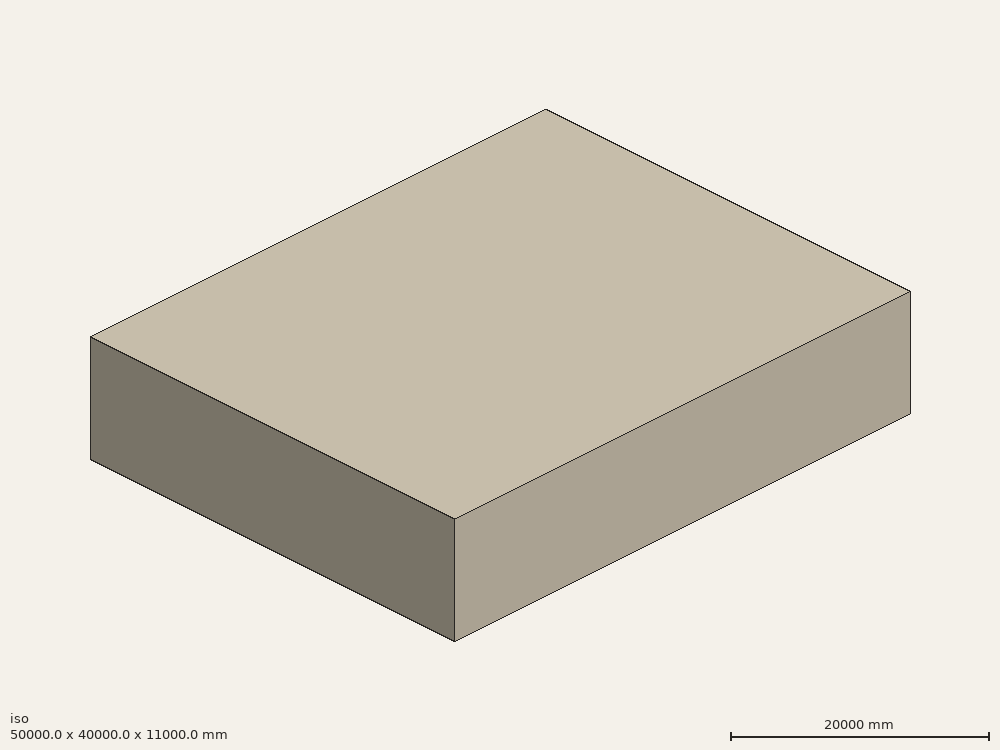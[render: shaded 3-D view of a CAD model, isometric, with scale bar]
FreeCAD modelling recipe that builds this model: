
FCSTD DOCUMENT  (FreeCAD 0.20R29603 (Git))
Label: windforces_cfMesh_hause
License: All rights reserved
LicenseURL: http://en.wikipedia.org/wiki/All_rights_reserved
objects: Part::FeaturePython×10, Part::Feature×4, Part::Box×3, App::DocumentObjectGroupPython×2, Mesh::Feature×1, Part::MultiFuse×1, Part::Cut×1, App::MaterialObjectPython×1
note: 19 computed .brp shape members not serialized (recipe doc carries the construction recipe); baked Part::Feature solids carry a one-line shape summary decoded from their .brp

FEATURE [Mesh::Feature] cfdwindforce
FEATURE [Part::Feature] cfdwindforce001
  shape: bbox 15090 x 17300 x 3871 mm, 94 faces, 0 solids (baked)
FEATURE [Part::Feature] cfdwindforce001_solid  label="cfdwindforce001 (Solid)"
  Placement = pos=(-7500,-8500,0) rot=(0,0,1;0rad)
  shape: bbox 15090 x 17300 x 3871 mm, 94 faces (baked)
FEATURE [Part::Box] Box  label="Cube"
  AttacherType = Attacher::AttachEngine3D
  Height = 11000
  Length = 50000
  Placement = pos=(-25000,-20000,0) rot=(0,0,1;0rad)
  Width = 40000
FEATURE [Part::Box] Box001  label="Cube001"
  AttacherType = Attacher::AttachEngine3D
  Height = 1400
  Length = 70
  Placement = pos=(4750,-7000,4000) rot=(0,1,0;1.0472rad)
  Width = 15000
FEATURE [Part::Feature] Box001001  label="Cube002"
  Placement = pos=(250,-7000,4000) rot=(0,1,0;1.0472rad)
  shape: bbox 1247 x 15000 x 760.6 mm, 6 faces (baked)
FEATURE [Part::Feature] Box001002  label="Cube003"
  Placement = pos=(2500,-7000,4000) rot=(0,1,0;1.0472rad)
  shape: bbox 1247 x 15000 x 760.6 mm, 6 faces (baked)
FEATURE [Part::Box] Box001003  label="refinement"
  AttacherType = Attacher::AttachEngine3D
  Height = 7000
  Length = 20000
  Placement = pos=(-10000,-11000,0) rot=(0,0,1;0rad)
  Width = 22000
FEATURE [Part::MultiFuse] Fusion
  Shapes = -> [cfdwindforce001_solid,Box001,Box001001,Box001002]
FEATURE [Part::Cut] Cut  label="building_model"
  Base = -> Box
  Tool = -> Fusion
FEATURE [Part::FeaturePython] PhysicsModel  # WARN: FeaturePython — macro-defined, semantics opaque (R4)
  Flow = 0
  Phase = 0
  SRFModelAxis = (0,0,0)
  SRFModelCoR = (0,0,0)
  SRFModelEnabled = false
  SRFModelRPM = 0
  Time = 0
  Turbulence = 3
  TurbulenceModel = 1
  gx = 0
  gy = -9800
  gz = 0
FEATURE [App::MaterialObjectPython] FluidProperties  # material (typed FeaturePython)
  Category = 1
  Material = CardName=AirIsothermal; Density=1.20 kg/m^3; Description=Standard air properties at 20 Degrees Celsius and 1 atm; DynamicViscosity=1.80e-5 kg/m/s; Name=Air; Type=Isothermal
FEATURE [Part::FeaturePython] InitialiseFields  # WARN: FeaturePython — macro-defined, semantics opaque (R4)
  PotentialFlow = true
  PotentialFlowP = true
  Pressure = 100
  ReThetat = 1
  Temperature = 290
  UseInletTemperatureValue = false
  UseInletTurbulenceValues = false
  UseInletUValues = false
  UseOutletPValue = false
  Ux = 0
  Uy = 0
  Uz = 0
  epsilon = 50000000
  gammaInt = 1
  k = 10000
  nuTilda = 55000000
  nut = 50000000
  omega = 1
FEATURE [Part::FeaturePython] CfdSolver  # WARN: FeaturePython — macro-defined, semantics opaque (R4)
  ConvergenceTol = 0.001
  EndTime = 1
  InputCaseName = case
  MaxCFLNumber = 5
  MaxInterfaceCFLNumber = 5
  MaxIterations = 2000
  Parallel = true
  ParallelCores = 4
  PurgeWrite = 0
  StartFrom = 0
  SteadyWriteInterval = 100
  TimeStep = 0.001
  TransientWriteInterval = 0.1
FEATURE [Part::FeaturePython] MeshRefinement  # WARN: FeaturePython — macro-defined, semantics opaque (R4)
  ExpansionRatio = 1
  Extrusion = false
  ExtrusionAngle = 5
  ExtrusionAxisDirection = (1,0,0)
  ExtrusionAxisPoint = (0,0,0)
  ExtrusionLayers = 1
  ExtrusionRatio = 1
  ExtrusionThickness = 1
  ExtrusionType = 2DPlanar
  FirstLayerHeight = 0
  Internal = true
  KeepExistingMesh = false
  NumberLayers = 0
  RefinementThickness = 0
  RegionEdgeRefinement = 1
  RelativeLength = 0.5
  ShapeRefs = -> [Box001003]
FEATURE [Part::FeaturePython] MeshRefinement001  # WARN: FeaturePython — macro-defined, semantics opaque (R4)
  ExpansionRatio = 1
  Extrusion = false
  ExtrusionAngle = 5
  ExtrusionAxisDirection = (1,0,0)
  ExtrusionAxisPoint = (0,0,0)
  ExtrusionLayers = 1
  ExtrusionRatio = 1
  ExtrusionThickness = 1
  ExtrusionType = 2DPlanar
  FirstLayerHeight = 0
  Internal = false
  KeepExistingMesh = false
  NumberLayers = 0
  RefinementThickness = 0
  RegionEdgeRefinement = 1
  RelativeLength = 0.5
  ShapeRefs = -> [Cut]
FEATURE [Part::FeaturePython] CfdFluidBoundary  label="inlet"  # WARN: FeaturePython — macro-defined, semantics opaque (R4)
  BoundarySubType = 5
  BoundaryType = 1
  DefaultBoundary = false
  DissipationRate = 50000000
  HeatFlux = 0
  HeatTransferCoeff = 0
  Intermittency = 1
  MassFlowRate = 0
  NuTilda = 55000000
  PeriodicCentreOfRotation = (0,0,0)
  PeriodicCentreOfRotationAxis = (0,0,0)
  PeriodicMaster = true
  PeriodicSeparationVector = (0,0,0)
  PorousBaffleMethod = 0
  Pressure = 100
  PressureDropCoeff = 0
  ReThetat = 1
  RelativeToFrame = false
  ReverseNormal = false
  RotationalPeriodic = false
  RoughnessConstant = 0.5
  RoughnessHeight = 0
  ScreenSpacing = 2
  ScreenWireDiameter = 0.2
  ShapeRefs = -> [Cut]
  SlipRatio = 0
  SpecificDissipationRate = 1
  Temperature = 290
  ThermalBoundaryType = 0
  TurbulenceInletSpecification = 0
  TurbulenceIntensityPercentage = 1
  TurbulenceLengthScale = 100
  TurbulentKineticEnergy = 10000
  TurbulentViscosity = 50000000
  Ux = -10
  Uy = 0
  Uz = 0
  VelocityIsCartesian = true
  VelocityMag = 0
  VolFlowRate = 0
  kEqnTurbulentKineticEnergy = 10000
  kEqnTurbulentViscosity = 50000000
FEATURE [Part::FeaturePython] CfdFluidBoundary001  label="open"  # WARN: FeaturePython — macro-defined, semantics opaque (R4)
  BoundarySubType = 13
  BoundaryType = 3
  DefaultBoundary = false
  DissipationRate = 50000000
  HeatFlux = 0
  HeatTransferCoeff = 0
  Intermittency = 1
  MassFlowRate = 0
  NuTilda = 55000000
  PeriodicCentreOfRotation = (0,0,0)
  PeriodicCentreOfRotationAxis = (0,0,0)
  PeriodicMaster = true
  PeriodicSeparationVector = (0,0,0)
  PorousBaffleMethod = 0
  Pressure = 100
  PressureDropCoeff = 0
  ReThetat = 1
  RelativeToFrame = false
  ReverseNormal = false
  RotationalPeriodic = false
  RoughnessConstant = 0.5
  RoughnessHeight = 0
  ScreenSpacing = 2
  ScreenWireDiameter = 0.2
  ShapeRefs = -> [Cut]
  SlipRatio = 0
  SpecificDissipationRate = 1
  Temperature = 290
  ThermalBoundaryType = 0
  TurbulenceInletSpecification = 0
  TurbulenceIntensityPercentage = 1
  TurbulenceLengthScale = 100
  TurbulentKineticEnergy = 10000
  TurbulentViscosity = 50000000
  Ux = 0
  Uy = 0
  Uz = 0
  VelocityIsCartesian = true
  VelocityMag = 0
  VolFlowRate = 0
  kEqnTurbulentKineticEnergy = 10000
  kEqnTurbulentViscosity = 50000000
FEATURE [Part::FeaturePython] CfdFluidBoundary002  label="ground"  # WARN: FeaturePython — macro-defined, semantics opaque (R4)
  BoundarySubType = 0
  BoundaryType = 0
  DefaultBoundary = false
  DissipationRate = 50000000
  HeatFlux = 0
  HeatTransferCoeff = 0
  Intermittency = 1
  MassFlowRate = 0
  NuTilda = 55000000
  PeriodicCentreOfRotation = (0,0,0)
  PeriodicCentreOfRotationAxis = (0,0,0)
  PeriodicMaster = true
  PeriodicSeparationVector = (0,0,0)
  PorousBaffleMethod = 0
  Pressure = 100
  PressureDropCoeff = 0
  ReThetat = 1
  RelativeToFrame = false
  ReverseNormal = false
  RotationalPeriodic = false
  RoughnessConstant = 0.5
  RoughnessHeight = 0
  ScreenSpacing = 2
  ScreenWireDiameter = 0.2
  ShapeRefs = -> [Cut]
  SlipRatio = 0
  SpecificDissipationRate = 1
  Temperature = 290
  ThermalBoundaryType = 0
  TurbulenceInletSpecification = 0
  TurbulenceIntensityPercentage = 1
  TurbulenceLengthScale = 100
  TurbulentKineticEnergy = 10000
  TurbulentViscosity = 50000000
  Ux = 0
  Uy = 0
  Uz = 0
  VelocityIsCartesian = true
  VelocityMag = 0
  VolFlowRate = 0
  kEqnTurbulentKineticEnergy = 10000
  kEqnTurbulentViscosity = 50000000
FEATURE [Part::FeaturePython] CfdFluidBoundary003  label="wall"  # WARN: FeaturePython — macro-defined, semantics opaque (R4)
  BoundarySubType = 0
  BoundaryType = 0
  DefaultBoundary = false
  DissipationRate = 50000000
  HeatFlux = 0
  HeatTransferCoeff = 0
  Intermittency = 1
  MassFlowRate = 0
  NuTilda = 55000000
  PeriodicCentreOfRotation = (0,0,0)
  PeriodicCentreOfRotationAxis = (0,0,0)
  PeriodicMaster = true
  PeriodicSeparationVector = (0,0,0)
  PorousBaffleMethod = 0
  Pressure = 100
  PressureDropCoeff = 0
  ReThetat = 1
  RelativeToFrame = false
  ReverseNormal = false
  RotationalPeriodic = false
  RoughnessConstant = 0.5
  RoughnessHeight = 0
  ScreenSpacing = 2
  ScreenWireDiameter = 0.2
  ShapeRefs = -> [Cut]
  SlipRatio = 0
  SpecificDissipationRate = 1
  Temperature = 290
  ThermalBoundaryType = 0
  TurbulenceInletSpecification = 0
  TurbulenceIntensityPercentage = 1
  TurbulenceLengthScale = 100
  TurbulentKineticEnergy = 10000
  TurbulentViscosity = 50000000
  Ux = 0
  Uy = 0
  Uz = 0
  VelocityIsCartesian = true
  VelocityMag = 0
  VolFlowRate = 0
  kEqnTurbulentKineticEnergy = 10000
  kEqnTurbulentViscosity = 50000000
FEATURE [Part::FeaturePython] MeshRefinement002  # WARN: FeaturePython — macro-defined, semantics opaque (R4)
  ExpansionRatio = 1
  Extrusion = false
  ExtrusionAngle = 5
  ExtrusionAxisDirection = (1,0,0)
  ExtrusionAxisPoint = (0,0,0)
  ExtrusionLayers = 1
  ExtrusionRatio = 1
  ExtrusionThickness = 1
  ExtrusionType = 2DPlanar
  FirstLayerHeight = 0
  Internal = false
  KeepExistingMesh = false
  NumberLayers = 1
  RefinementThickness = 0
  RegionEdgeRefinement = 1
  RelativeLength = 0.1
  ShapeRefs = -> [Cut]
FEATURE [App::DocumentObjectGroupPython] Cut_Mesh  # scripted group (container) (typed FeaturePython)
  CaseName = meshCase
  CellsBetweenLevels = 3
  CharacteristicLengthMax = 2000
  ConvertToDualMesh = false
  EdgeRefinement = 1
  ElementDimension = 1
  Group = -> [MeshRefinement,MeshRefinement001,MeshRefinement002]
  ImplicitEdgeDetection = false
  MeshUtility = 0
  NumberOfProcesses = 1
  NumberOfThreads = 0
  Part = -> Cut
  PointInMesh = x=0.0 mm; y=0.0 mm; z=0.0 mm
  STLAngularMeshDensity = 100
  STLRelativeLinearDeflection = 0.001
FEATURE [App::DocumentObjectGroupPython] CfdAnalysis  # scripted group (container) (typed FeaturePython)
  Group = -> [PhysicsModel,FluidProperties,InitialiseFields,CfdSolver,Cut_Mesh,CfdFluidBoundary,CfdFluidBoundary001,CfdFluidBoundary002,CfdFluidBoundary003]
  IsActiveAnalysis = true
  NeedsCaseRewrite = true
  NeedsMeshRerun = false
  NeedsMeshRewrite = false
